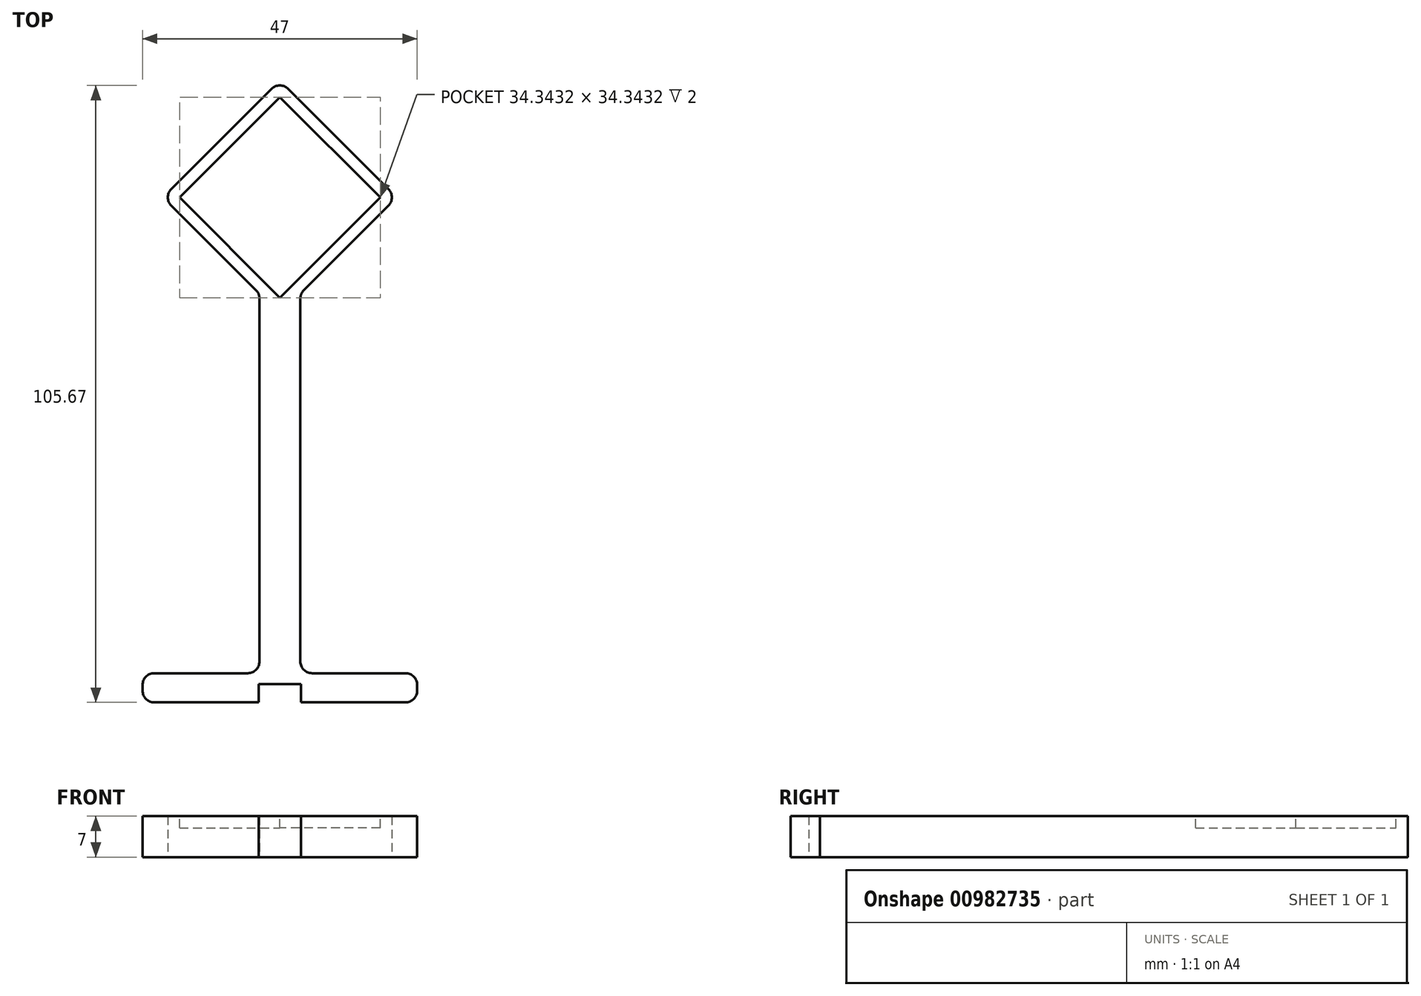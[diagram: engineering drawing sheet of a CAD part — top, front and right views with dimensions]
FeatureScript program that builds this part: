
annotation { "Feature Type Name" : "Feature", "Feature Type Description" : "" }
export const myFeature = defineFeature(function(context is Context, id is Id, definition is map)
    precondition{}
    {
        {
            var Q0;
            Q0=qCreatedBy(makeId("Top.planeOp"),FACE);
            var sketch = newSketch(context, id + "F0", { "sketchPlane" : qUnion([Q0])});
            skLineSegment(sketch, "E0", {"start": v(-3.5, -0.5) * mm, "end": v(-3.5, -65.5) * mm});
            skLineSegment(sketch, "E1", {"start": v(-3.5, -65.5) * mm, "end": v(-23.5, -65.5) * mm});
            skLineSegment(sketch, "E2", {"start": v(-23.5, -65.5) * mm, "end": v(-23.5, -70.5) * mm});
            skLineSegment(sketch, "E3", {"start": v(-23.5, -70.5) * mm, "end": v(23.5, -70.5) * mm});
            skLineSegment(sketch, "E4", {"start": v(23.5, -70.5) * mm, "end": v(23.5, -65.5) * mm});
            skLineSegment(sketch, "E5", {"start": v(23.5, -65.5) * mm, "end": v(3.5, -65.5) * mm});
            skLineSegment(sketch, "E6", {"start": v(3.5, -65.5) * mm, "end": v(3.5, -0.5) * mm});
            skLineSegment(sketch, "E7.bottom", {"start": v(3.6, -70.5) * mm, "end": v(-3.6, -70.5) * mm});
            skLineSegment(sketch, "E7.top", {"start": v(3.6, -67.4) * mm, "end": v(-3.6, -67.4) * mm});
            skLineSegment(sketch, "E7.left", {"start": v(3.6, -70.5) * mm, "end": v(3.6, -67.4) * mm});
            skLineSegment(sketch, "E7.right", {"start": v(-3.6, -70.5) * mm, "end": v(-3.6, -67.4) * mm});
            skPoint(sketch, "E7.middle", {"position": v(0, -68.95) * mm});
            skLineSegment(sketch, "E8.bottom", {"start": v(-23.5, -70.5) * mm, "end": v(-17.5, -70.5) * mm});
            skLineSegment(sketch, "E8.top", {"start": v(-23.5, -70.8) * mm, "end": v(-17.5, -70.8) * mm});
            skLineSegment(sketch, "E8.left", {"start": v(-23.5, -70.5) * mm, "end": v(-23.5, -70.8) * mm});
            skLineSegment(sketch, "E8.right", {"start": v(-17.5, -70.5) * mm, "end": v(-17.5, -70.8) * mm});
            skLineSegment(sketch, "E9.MirrorCS", {"start": v(23.5, -70.5) * mm, "end": v(17.5, -70.5) * mm});
            skLineSegment(sketch, "E10.MirrorCS", {"start": v(17.5, -70.5) * mm, "end": v(17.5, -70.8) * mm});
            skLineSegment(sketch, "E11.MirrorCS", {"start": v(23.5, -70.8) * mm, "end": v(17.5, -70.8) * mm});
            skLineSegment(sketch, "E12.MirrorCS", {"start": v(23.5, -70.5) * mm, "end": v(23.5, -70.8) * mm});
            skLineSegment(sketch, "E13", {"start": v(0, 36) * mm, "end": v(-20, 16) * mm});
            skLineSegment(sketch, "E14", {"start": v(-20, 16) * mm, "end": v(0, -4) * mm});
            skLineSegment(sketch, "E15", {"start": v(0, -4) * mm, "end": v(20, 16) * mm});
            skLineSegment(sketch, "E16", {"start": v(20, 16) * mm, "end": v(0, 36) * mm});
            skSolve(sketch);
        }
        {
            var Q0;
            {var subQ0=sQuery(id+"F0.wireOp",EDGE,"im0v1Rov-prSM-cwdN-f0IW-ScqFdnQkXUSi");Q0=makeQuery(id+"F0.imprint","IMPRINT",FACE,{"disambiguationData":[TD([[makeQuery(id+"F0.imprint","IMPRINT",EDGE,{"derivedFrom":subQ0}),1.0]])]});}
            var Q1;
            {var subQ7=sQuery(id+"F0.wireOp",EDGE,"E0");Q1=makeQuery(id+"F0.imprint","IMPRINT",FACE,{"disambiguationData":[TD([[makeQuery(id+"F0.imprint","IMPRINT",EDGE,{"derivedFrom":subQ7}),1.0]])]});}
            var Q2;
            Q2=makeQuery(id+"F0.imprint","IMPRINT",FACE,{"disambiguationData":[TD([[makeQuery(id+"F0.imprint","IMPRINT",EDGE,{"derivedFrom":sQuery(id+"F0.wireOp",EDGE,"E8.bottom")}),-1.0]])]});
            var Q3;
            Q3=makeQuery(id+"F0.imprint","IMPRINT",FACE,{"disambiguationData":[TD([[makeQuery(id+"F0.imprint","IMPRINT",EDGE,{"derivedFrom":sQuery(id+"F0.wireOp",EDGE,"E9.MirrorCS")}),1.0]])]});
            var Q4;
            {var subQ5=sQuery(id+"F0.wireOp",EDGE,"E13");Q4=makeQuery(id+"F0.imprint","IMPRINT",FACE,{"disambiguationData":[TD([[makeQuery(id+"F0.imprint","IMPRINT",EDGE,{"derivedFrom":subQ5}),1.0]])]});}
            extrude(context, id + "F1", {"entities" : qUnion([Q0, Q1, Q2, Q3, Q4]), "depth" : 7 * mm, "offsetDistance" : 25 * mm});
        }
        {
            var Q0;
            Q0=makeQuery(id+"F1.opExtrude","CAP_FACE",FACE,{"disambiguationData":[OSD([sQuery(id+"F0.wireOp",EDGE,"E0"),sQuery(id+"F0.wireOp",EDGE,"E1"),sQuery(id+"F0.wireOp",EDGE,"E2"),sQuery(id+"F0.wireOp",EDGE,"E3"),sQuery(id+"F0.wireOp",EDGE,"E4"),sQuery(id+"F0.wireOp",EDGE,"E5"),sQuery(id+"F0.wireOp",EDGE,"E6"),sQuery(id+"F0.wireOp",EDGE,"E7.top"),sQuery(id+"F0.wireOp",EDGE,"E7.left"),sQuery(id+"F0.wireOp",EDGE,"E7.right"),sQuery(id+"F0.wireOp",EDGE,"E8.top"),sQuery(id+"F0.wireOp",EDGE,"E8.left"),sQuery(id+"F0.wireOp",EDGE,"E8.right"),sQuery(id+"F0.wireOp",EDGE,"E10.MirrorCS"),sQuery(id+"F0.wireOp",EDGE,"E11.MirrorCS"),sQuery(id+"F0.wireOp",EDGE,"E12.MirrorCS"),sQuery(id+"F0.wireOp",EDGE,"E13"),sQuery(id+"F0.wireOp",EDGE,"E14"),sQuery(id+"F0.wireOp",EDGE,"E15"),sQuery(id+"F0.wireOp",EDGE,"E16")])],"isStart":false});
            var sketch = newSketch(context, id + "F2", { "sketchPlane" : qUnion([Q0])});
            skLineSegment(sketch, "E17", {"start": v(-17.17, 16) * mm, "end": v(0, 33.17) * mm});
            skLineSegment(sketch, "E18", {"start": v(0, 33.17) * mm, "end": v(17.17, 16) * mm});
            skLineSegment(sketch, "E19", {"start": v(17.17, 16) * mm, "end": v(0, -1.17) * mm});
            skLineSegment(sketch, "E20", {"start": v(0, -1.17) * mm, "end": v(-17.17, 16) * mm});
            skSolve(sketch);
        }
        {
            var Q0;
            Q0=makeQuery(id+"F2.imprint","IMPRINT",FACE,{"disambiguationData":[TD([[makeQuery(id+"F2.imprint","IMPRINT",EDGE,{"derivedFrom":sQuery(id+"F2.wireOp",EDGE,"E17")}),-1.0]])]});
            extrude(context, id + "F3", {"entities" : qUnion([Q0]), "operationType" : NewBodyOperationType.REMOVE, "oppositeDirection" : true, "depth" : 2 * mm, "offsetDistance" : 25 * mm});
        }
        {
            var Q0;
            Q0=makeQuery(id+"F1.opExtrude","SWEPT_EDGE",EDGE,{"disambiguationData":[OSD([sQuery(id+"F0.wireOp",EDGE,"0U4RxweM-u2bA-2Qqt-OOBg-x1ftkZs6jUrD"),sQuery(id+"F0.wireOp",EDGE,"E0")])]});
            var Q1;
            Q1=makeQuery(id+"F1.opExtrude","SWEPT_EDGE",EDGE,{"disambiguationData":[OSD([sQuery(id+"F0.wireOp",EDGE,"0U4RxweM-u2bA-2Qqt-OOBg-x1ftkZs6jUrD"),sQuery(id+"F0.wireOp",EDGE,"E6")])]});
            var Q2;
            Q2=makeQuery(id+"F1.opExtrude","SWEPT_EDGE",EDGE,{"disambiguationData":[OSD([sQuery(id+"F0.wireOp",EDGE,"0U4RxweM-u2bA-2Qqt-OOBg-x1ftkZs6jUrD"),sQuery(id+"F0.wireOp",EDGE,"im0v1Rov-prSM-cwdN-f0IW-ScqFdnQkXUSi")])]});
            var Q3;
            Q3=makeQuery(id+"F1.opExtrude","SWEPT_EDGE",EDGE,{"disambiguationData":[OSD([sQuery(id+"F0.wireOp",EDGE,"0U4RxweM-u2bA-2Qqt-OOBg-x1ftkZs6jUrD"),sQuery(id+"F0.wireOp",EDGE,"IfBi3EXo-PReU-dRJG-joro-0UU4bWJMkuGZ")])]});
            var Q4;
            Q4=makeQuery(id+"F1.opExtrude","SWEPT_EDGE",EDGE,{"disambiguationData":[OSD([sQuery(id+"F0.wireOp",EDGE,"im0v1Rov-prSM-cwdN-f0IW-ScqFdnQkXUSi"),sQuery(id+"F0.wireOp",EDGE,"IfBi3EXo-PReU-dRJG-joro-0UU4bWJMkuGZ")])]});
            var Q5;
            Q5=makeQuery(id+"F1.opExtrude","SWEPT_EDGE",EDGE,{"disambiguationData":[OSD([sQuery(id+"F0.wireOp",EDGE,"E5"),sQuery(id+"F0.wireOp",EDGE,"E6")])]});
            var Q6;
            Q6=makeQuery(id+"F1.opExtrude","SWEPT_EDGE",EDGE,{"disambiguationData":[OSD([sQuery(id+"F0.wireOp",EDGE,"E0"),sQuery(id+"F0.wireOp",EDGE,"E1")])]});
            var Q7;
            Q7=makeQuery(id+"F1.opExtrude","SWEPT_EDGE",EDGE,{"disambiguationData":[OSD([sQuery(id+"F0.wireOp",EDGE,"E1"),sQuery(id+"F0.wireOp",EDGE,"E2")])]});
            var Q8;
            Q8=makeQuery(id+"F1.opExtrude","SWEPT_EDGE",EDGE,{"disambiguationData":[OSD([sQuery(id+"F0.wireOp",EDGE,"E4"),sQuery(id+"F0.wireOp",EDGE,"E5")])]});
            var Q9;
            Q9=makeQuery(id+"F1.opExtrude","SWEPT_EDGE",EDGE,{"disambiguationData":[OSD([sQuery(id+"F0.wireOp",EDGE,"E8.top"),sQuery(id+"F0.wireOp",EDGE,"E8.left")])]});
            var Q10;
            Q10=makeQuery(id+"F1.opExtrude","SWEPT_EDGE",EDGE,{"disambiguationData":[OSD([sQuery(id+"F0.wireOp",EDGE,"E11.MirrorCS"),sQuery(id+"F0.wireOp",EDGE,"E12.MirrorCS")])]});
            var Q11;
            Q11=makeQuery(id+"F1.opExtrude","SWEPT_EDGE",EDGE,{"disambiguationData":[OSD([sQuery(id+"F0.wireOp",EDGE,"E15"),sQuery(id+"F0.wireOp",EDGE,"E16")])]});
            var Q12;
            Q12=makeQuery(id+"F1.opExtrude","SWEPT_EDGE",EDGE,{"disambiguationData":[OSD([sQuery(id+"F0.wireOp",EDGE,"E13"),sQuery(id+"F0.wireOp",EDGE,"E16")])]});
            var Q13;
            Q13=makeQuery(id+"F1.opExtrude","SWEPT_EDGE",EDGE,{"disambiguationData":[OSD([sQuery(id+"F0.wireOp",EDGE,"E13"),sQuery(id+"F0.wireOp",EDGE,"E14")])]});
            fillet(context, id + "F4", {"entities" : qUnion([Q0, Q1, Q2, Q3, Q4, Q5, Q6, Q7, Q8, Q9, Q10, Q11, Q12, Q13]), "radius" : 2 * mm, "tangentPropagation" : true, "allowEdgeOverflow" : false});
        }
    });
